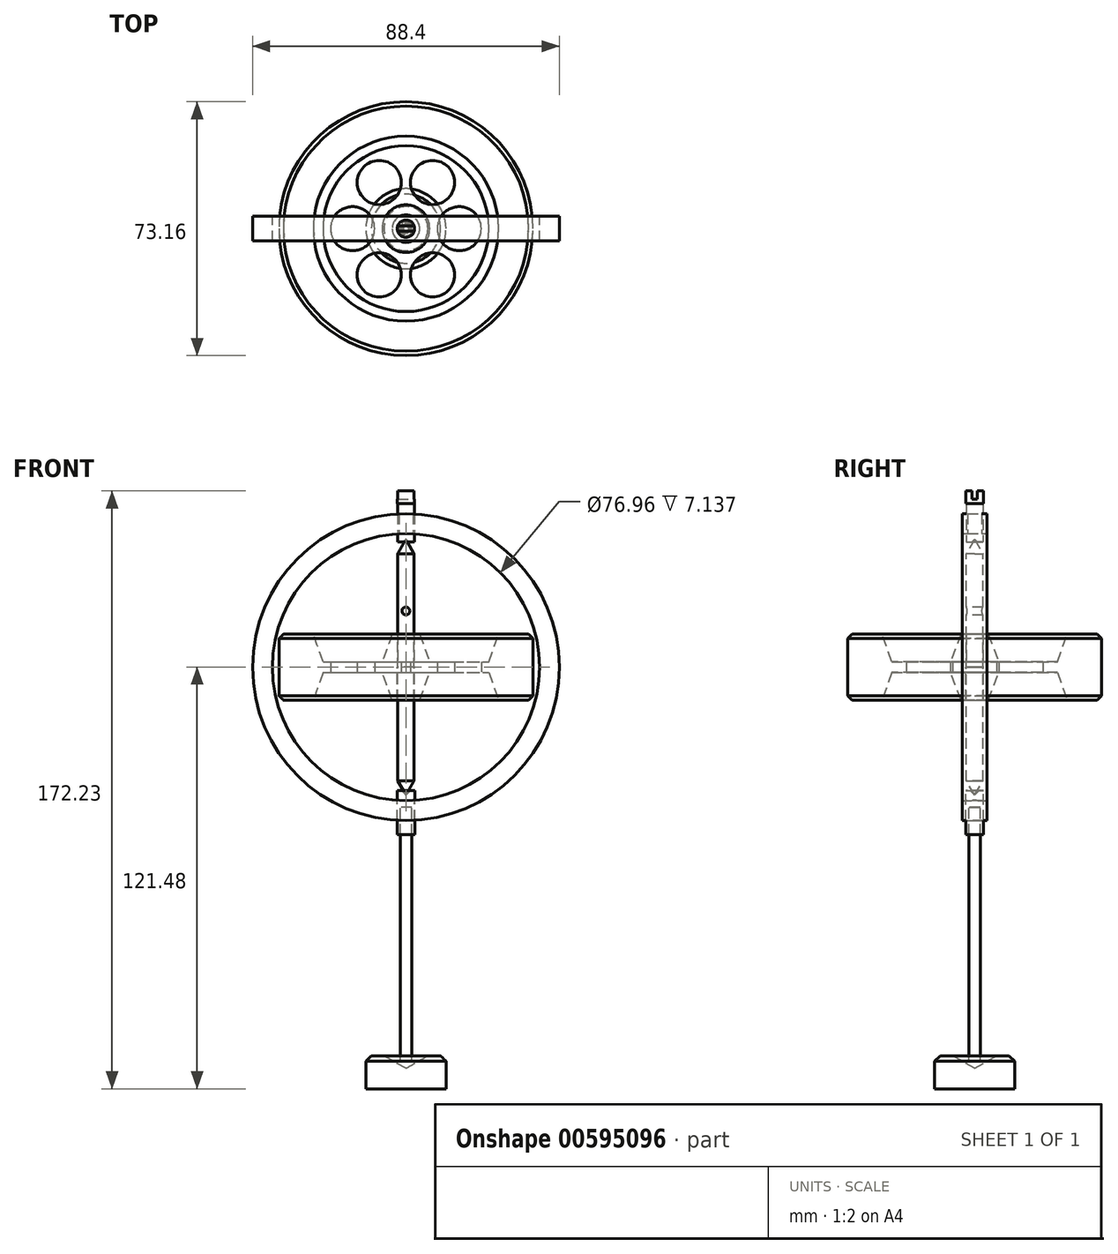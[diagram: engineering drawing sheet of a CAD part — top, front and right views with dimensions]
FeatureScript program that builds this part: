
annotation { "Feature Type Name" : "Feature", "Feature Type Description" : "" }
export const myFeature = defineFeature(function(context is Context, id is Id, definition is map)
    precondition{}
    {
        {
            var Q0;
            Q0=qCreatedBy(makeId("Front.planeOp"),FACE);
            var sketch = newSketch(context, id + "F0", { "sketchPlane" : qUnion([Q0])});
            skLineSegment(sketch, "E0.bottom", {"start": v(0, -9.52) * mm, "end": v(36.58, -9.52) * mm, "construction": true});
            skLineSegment(sketch, "E0.top", {"start": v(0, 9.52) * mm, "end": v(36.58, 9.52) * mm, "construction": true});
            skLineSegment(sketch, "E0.left", {"start": v(0, -9.52) * mm, "end": v(0, 9.52) * mm, "construction": true});
            skLineSegment(sketch, "E0.right", {"start": v(36.58, -9.52) * mm, "end": v(36.58, 9.52) * mm});
            skLineSegment(sketch, "E1", {"start": v(0, 0) * mm, "end": v(36.58, 0) * mm, "construction": true});
            skLineSegment(sketch, "E2", {"start": v(6.86, 1.57) * mm, "end": v(6.86, -1.57) * mm, "construction": true});
            skPoint(sketch, "E3", {"position": v(6.86, 0) * mm});
            skLineSegment(sketch, "E4", {"start": v(6.86, -1.57) * mm, "end": v(3.96, -9.53) * mm});
            skLineSegment(sketch, "E5.MirrorCS", {"start": v(6.86, 1.57) * mm, "end": v(3.96, 9.52) * mm});
            skLineSegment(sketch, "E6", {"start": v(2.39, 9.52) * mm, "end": v(2.39, -9.52) * mm});
            skLineSegment(sketch, "E7", {"start": v(6.86, 1.57) * mm, "end": v(23.88, 1.57) * mm});
            skLineSegment(sketch, "E8", {"start": v(2.39, 9.52) * mm, "end": v(3.96, 9.52) * mm});
            skLineSegment(sketch, "E9", {"start": v(2.39, -9.52) * mm, "end": v(3.96, -9.52) * mm});
            skLineSegment(sketch, "E10", {"start": v(26.67, -9.52) * mm, "end": v(36.58, -9.52) * mm});
            skLineSegment(sketch, "E11", {"start": v(26.67, 9.52) * mm, "end": v(36.58, 9.52) * mm});
            skLineSegment(sketch, "E12", {"start": v(23.88, -1.57) * mm, "end": v(26.67, -9.53) * mm});
            skLineSegment(sketch, "E13", {"start": v(6.86, -1.57) * mm, "end": v(23.88, -1.57) * mm});
            skLineSegment(sketch, "E14", {"start": v(26.67, 9.52) * mm, "end": v(23.88, 1.57) * mm});
            skSolve(sketch);
        }
        {
            var Q0;
            Q0=makeQuery(id+"F0.imprint","IMPRINT",FACE,{"disambiguationData":[TD([[makeQuery(id+"F0.imprint","IMPRINT",EDGE,{"derivedFrom":sQuery(id+"F0.wireOp",EDGE,"E0.right")}),1.0]])]});
            var Q1;
            Q1=sQuery(id+"F0.wireOp",EDGE,"E0.left");
            revolve(context, id + "F1", {"entities" : qUnion([Q0]), "axis" : qUnion([Q1]), "revolveType" : RevolveType.FULL});
        }
        {
            var Q0;
            Q0=qCreatedBy(makeId("Top.planeOp"),FACE);
            var sketch = newSketch(context, id + "F2", { "sketchPlane" : qUnion([Q0])});
            skPoint(sketch, "E15.0", {"position": v(36.58, 0) * mm});
            skCircle(sketch, "E16.cCircle", {"center": v(0, 0) * mm, "radius": 36.58 * mm, "construction": true});
            skPoint(sketch, "E17.0", {"position": v(23.88, 0) * mm});
            skPoint(sketch, "E18.0", {"position": v(6.86, 0) * mm});
            skCircle(sketch, "E19.cCircle", {"center": v(0, 0) * mm, "radius": 31.68 * mm, "construction": true});
            skLineSegment(sketch, "E19.0", {"start": v(36.58, 0) * mm, "end": v(18.29, -31.68) * mm, "construction": true});
            skLineSegment(sketch, "E19.1", {"start": v(18.29, -31.68) * mm, "end": v(-18.29, -31.68) * mm, "construction": true});
            skLineSegment(sketch, "E19.2", {"start": v(-18.29, -31.68) * mm, "end": v(-36.58, 0) * mm, "construction": true});
            skLineSegment(sketch, "E19.3", {"start": v(-36.58, 0) * mm, "end": v(-18.29, 31.68) * mm, "construction": true});
            skLineSegment(sketch, "E19.4", {"start": v(-18.29, 31.68) * mm, "end": v(18.29, 31.68) * mm, "construction": true});
            skLineSegment(sketch, "E19.5", {"start": v(18.29, 31.68) * mm, "end": v(36.58, 0) * mm, "construction": true});
            skPoint(sketch, "E19.0.midPoint", {"position": v(27.43, -15.84) * mm});
            skLineSegment(sketch, "E20", {"start": v(0, 0) * mm, "end": v(36.58, 0) * mm, "construction": true});
            skCircle(sketch, "E21", {"center": v(15.37, 0) * mm, "radius": 6.35 * mm});
            skLineSegment(sketch, "E22", {"start": v(6.86, 0) * mm, "end": v(23.88, 0) * mm, "construction": true});
            skCircle(sketch, "E23.1.0", {"center": v(7.68, 13.3) * mm, "radius": 6.35 * mm});
            skCircle(sketch, "E23.2.0", {"center": v(-7.68, 13.3) * mm, "radius": 6.35 * mm});
            skCircle(sketch, "E23.3.0", {"center": v(-15.37, 0) * mm, "radius": 6.35 * mm});
            skCircle(sketch, "E23.4.0", {"center": v(-7.68, -13.3) * mm, "radius": 6.35 * mm});
            skCircle(sketch, "E23.5.0", {"center": v(7.68, -13.3) * mm, "radius": 6.35 * mm});
            skSolve(sketch);
        }
        {
            var Q0;
            Q0 = qSketchRegion(id + "F2", true);
            extrude(context, id + "F3", {"entities" : qUnion([Q0]), "operationType" : NewBodyOperationType.REMOVE, "endBound" : BoundingType.THROUGH_ALL, "depth" : 25.4 * mm, "offsetDistance" : 25.4 * mm, "hasSecondDirection" : true, "secondDirectionBound" : SecondDirectionBoundingType.THROUGH_ALL, "secondDirectionOppositeDirection" : true, "secondDirectionDepth" : 25.4 * mm});
        }
        {
            var Q0;
            Q0=qCreatedBy(makeId("Front.planeOp"),FACE);
            var sketch = newSketch(context, id + "F4", { "sketchPlane" : qUnion([Q0])});
            skCircle(sketch, "E24", {"center": v(0, 0) * mm, "radius": 44.2 * mm});
            skCircle(sketch, "E25", {"center": v(0, 0) * mm, "radius": 38.48 * mm});
            skSolve(sketch);
        }
        {
            var Q0;
            Q0=makeQuery(id+"F4.imprint","IMPRINT",FACE,{"disambiguationData":[TD([[makeQuery(id+"F4.imprint","IMPRINT",EDGE,{"derivedFrom":sQuery(id+"F4.wireOp",EDGE,"E24")}),1.0]])]});
            extrude(context, id + "F5", {"entities" : qUnion([Q0]), "endBound" : BoundingType.SYMMETRIC, "depth" : 7.14 * mm, "offsetDistance" : 25.4 * mm});
        }
        {
            var Q0;
            Q0=qCreatedBy(makeId("Top.planeOp"),FACE);
            var sketch = newSketch(context, id + "F6", { "sketchPlane" : qUnion([Q0])});
            skCircle(sketch, "E26", {"center": v(0, 0) * mm, "radius": 2.5 * mm});
            skSolve(sketch);
        }
        {
            var Q0;
            Q0 = qSketchRegion(id + "F6", true);
            extrude(context, id + "F7", {"entities" : qUnion([Q0]), "operationType" : NewBodyOperationType.REMOVE, "endBound" : BoundingType.THROUGH_ALL, "oppositeDirection" : true, "depth" : 25.4 * mm, "offsetDistance" : 25.4 * mm});
        }
        {
            var Q0;
            Q0=qCreatedBy(makeId("Top.planeOp"),FACE);
            var sketch = newSketch(context, id + "F8", { "sketchPlane" : qUnion([Q0])});
            skCircle(sketch, "E27", {"center": v(0, 0) * mm, "radius": 2.02 * mm});
            skSolve(sketch);
        }
        {
            var Q0;
            Q0 = qSketchRegion(id + "F8", true);
            extrude(context, id + "F9", {"entities" : qUnion([Q0]), "operationType" : NewBodyOperationType.REMOVE, "endBound" : BoundingType.THROUGH_ALL, "depth" : 25.4 * mm, "offsetDistance" : 25.4 * mm});
        }
        {
            var Q0;
            Q0=makeQuery(id+"F1.opRevolve","SWEPT_EDGE",EDGE,{"disambiguationData":[OSD([sQuery(id+"F0.wireOp",EDGE,"E0.right"),sQuery(id+"F0.wireOp",EDGE,"E11")])]});
            var Q1;
            Q1=makeQuery(id+"F1.opRevolve","SWEPT_EDGE",EDGE,{"disambiguationData":[OSD([sQuery(id+"F0.wireOp",EDGE,"E0.right"),sQuery(id+"F0.wireOp",EDGE,"E10")])]});
            chamfer(context, id + "F10", {"entities" : qUnion([Q0, Q1]), "width" : 1.27 * mm, "tangentPropagation" : true});
        }
        {
            var Q0;
            Q0=qCreatedBy(makeId("Front.planeOp"),FACE);
            var sketch = newSketch(context, id + "F11", { "sketchPlane" : qUnion([Q0])});
            skLineSegment(sketch, "E28.0", {"start": v(2.39, 9.52) * mm, "end": v(-2.39, 9.52) * mm, "construction": true});
            skLineSegment(sketch, "E29.left", {"start": v(0, 36.83) * mm, "end": v(0, -36.83) * mm});
            skLineSegment(sketch, "E29.right", {"start": v(2.39, 32.7) * mm, "end": v(2.39, -32.7) * mm});
            skLineSegment(sketch, "E30", {"start": v(0, 36.83) * mm, "end": v(2.39, 32.7) * mm});
            skLineSegment(sketch, "E31", {"start": v(0, -36.83) * mm, "end": v(2.39, -32.7) * mm});
            skSolve(sketch);
        }
        {
            var Q0;
            Q0=makeQuery(id+"F11.imprint","IMPRINT",FACE,{"disambiguationData":[TD([[makeQuery(id+"F11.imprint","IMPRINT",EDGE,{"derivedFrom":sQuery(id+"F11.wireOp",EDGE,"E29.left")}),1.0]])]});
            var Q1;
            Q1=sQuery(id+"F11.wireOp",EDGE,"E29.left");
            revolve(context, id + "F12", {"entities" : qUnion([Q0]), "axis" : qUnion([Q1]), "revolveType" : RevolveType.FULL});
        }
        {
            var Q0;
            Q0=qCreatedBy(makeId("Front.planeOp"),FACE);
            var sketch = newSketch(context, id + "F13", { "sketchPlane" : qUnion([Q0])});
            skPoint(sketch, "E32.0", {"position": v(0, 36.83) * mm});
            skPoint(sketch, "E33.0", {"position": v(0, -36.83) * mm});
            skCircle(sketch, "E34", {"center": v(0, 16.18) * mm, "radius": 1.14 * mm});
            skSolve(sketch);
        }
        {
            var Q0;
            Q0 = qSketchRegion(id + "F13", true);
            extrude(context, id + "F14", {"entities" : qUnion([Q0]), "operationType" : NewBodyOperationType.REMOVE, "oppositeDirection" : true, "depth" : 25.4 * mm, "offsetDistance" : 25.4 * mm, "hasSecondDirection" : true, "secondDirectionOppositeDirection" : false, "secondDirectionDepth" : 25.4 * mm});
        }
        {
            var Q0;
            Q0=qCreatedBy(makeId("Front.planeOp"),FACE);
            var sketch = newSketch(context, id + "F15", { "sketchPlane" : qUnion([Q0])});
            skPoint(sketch, "E35.0", {"position": v(0, -36.83) * mm});
            skLineSegment(sketch, "E36.bottom", {"start": v(0, -35.56) * mm, "end": v(2.54, -35.56) * mm});
            skLineSegment(sketch, "E36.top", {"start": v(0, -48.26) * mm, "end": v(2.54, -48.26) * mm});
            skLineSegment(sketch, "E36.left", {"start": v(0, -35.56) * mm, "end": v(0, -48.26) * mm});
            skLineSegment(sketch, "E36.right", {"start": v(2.54, -35.56) * mm, "end": v(2.54, -48.26) * mm});
            skLineSegment(sketch, "E37", {"start": v(0, -40.39) * mm, "end": v(1.65, -40.39) * mm});
            skLineSegment(sketch, "E38", {"start": v(1.65, -40.39) * mm, "end": v(1.65, -48.26) * mm});
            skLineSegment(sketch, "E39", {"start": v(0, -36.83) * mm, "end": v(1.27, -35.56) * mm});
            skSolve(sketch);
        }
        {
            var Q0;
            {var subQ0=sQuery(id+"F15.wireOp",EDGE,"E36.right");Q0=makeQuery(id+"F15.imprint","IMPRINT",FACE,{"disambiguationData":[TD([[makeQuery(id+"F15.imprint","IMPRINT",EDGE,{"derivedFrom":subQ0}),-1.0]])]});}
            var Q1;
            Q1=sQuery(id+"F15.wireOp",EDGE,"E36.left");
            revolve(context, id + "F16", {"entities" : qUnion([Q0]), "axis" : qUnion([Q1]), "revolveType" : RevolveType.FULL});
        }
        {
            var Q0;
            Q0=qCreatedBy(makeId("Front.planeOp"),FACE);
            var sketch = newSketch(context, id + "F17", { "sketchPlane" : qUnion([Q0])});
            skPoint(sketch, "E40.0", {"position": v(0, 36.83) * mm});
            skLineSegment(sketch, "E41.bottom", {"start": v(0, 36.04) * mm, "end": v(2.5, 36.04) * mm});
            skLineSegment(sketch, "E41.top", {"start": v(0, 50.75) * mm, "end": v(2.5, 50.75) * mm});
            skLineSegment(sketch, "E41.left", {"start": v(0, 36.04) * mm, "end": v(0, 50.75) * mm});
            skLineSegment(sketch, "E41.right", {"start": v(2.5, 36.04) * mm, "end": v(2.5, 50.75) * mm});
            skLineSegment(sketch, "E42", {"start": v(2.5, 47.17) * mm, "end": v(2.41, 47.17) * mm});
            skLineSegment(sketch, "E43", {"start": v(2.41, 47.17) * mm, "end": v(2.41, 36.04) * mm});
            skLineSegment(sketch, "E44", {"start": v(0, 36.83) * mm, "end": v(0.79, 36.04) * mm});
            skSolve(sketch);
        }
        {
            var Q0;
            {var subQ1=sQuery(id+"F17.wireOp",EDGE,"E41.top");Q0=makeQuery(id+"F17.imprint","IMPRINT",FACE,{"disambiguationData":[TD([[makeQuery(id+"F17.imprint","IMPRINT",EDGE,{"derivedFrom":subQ1}),-1.0]])]});}
            var Q1;
            Q1=sQuery(id+"F17.wireOp",EDGE,"E41.left");
            revolve(context, id + "F18", {"entities" : qUnion([Q0]), "axis" : qUnion([Q1]), "revolveType" : RevolveType.FULL});
        }
        {
            var Q0;
            Q0=makeQuery(id+"F16.opRevolve","SWEPT_FACE",FACE,{"disambiguationData":[OSD([sQuery(id+"F15.wireOp",EDGE,"E37")])]});
            extrude(context, id + "F19", {"entities" : qUnion([Q0]), "depth" : 73.15 * mm, "offsetDistance" : 25.4 * mm});
        }
        {
            var Q0;
            Q0=qCreatedBy(makeId("Front.planeOp"),FACE);
            var sketch = newSketch(context, id + "F20", { "sketchPlane" : qUnion([Q0])});
            skLineSegment(sketch, "E45.0", {"start": v(-1.65, -113.54) * mm, "end": v(1.65, -113.54) * mm, "construction": true});
            skPoint(sketch, "E46", {"position": v(0, -113.54) * mm});
            skLineSegment(sketch, "E47.bottom", {"start": v(0, -111.95) * mm, "end": v(-11.55, -111.95) * mm});
            skLineSegment(sketch, "E47.top", {"start": v(0, -121.48) * mm, "end": v(-11.55, -121.48) * mm});
            skLineSegment(sketch, "E47.left", {"start": v(0, -111.95) * mm, "end": v(0, -121.48) * mm});
            skLineSegment(sketch, "E47.right", {"start": v(-11.55, -111.95) * mm, "end": v(-11.55, -121.48) * mm});
            skLineSegment(sketch, "E48", {"start": v(-9.96, -111.95) * mm, "end": v(-11.55, -113.54) * mm});
            skLineSegment(sketch, "E49", {"start": v(0, -115.62) * mm, "end": v(-6.35, -111.95) * mm});
            skSolve(sketch);
        }
        {
            var Q0;
            {var subQ1=sQuery(id+"F20.wireOp",EDGE,"E47.top");Q0=makeQuery(id+"F20.imprint","IMPRINT",FACE,{"disambiguationData":[TD([[makeQuery(id+"F20.imprint","IMPRINT",EDGE,{"derivedFrom":subQ1}),-1.0]])]});}
            var Q1;
            Q1=sQuery(id+"F20.wireOp",EDGE,"E47.left");
            revolve(context, id + "F21", {"entities" : qUnion([Q0]), "axis" : qUnion([Q1]), "revolveType" : RevolveType.FULL});
        }
        {
            var Q0;
            Q0=makeQuery(id+"F18.opRevolve","SWEPT_FACE",FACE,{"disambiguationData":[OSD([sQuery(id+"F17.wireOp",EDGE,"E41.top")])]});
            var sketch = newSketch(context, id + "F22", { "sketchPlane" : qUnion([Q0])});
            skLineSegment(sketch, "E50.bottom", {"start": v(-2.93, 0.76) * mm, "end": v(2.93, 0.76) * mm});
            skLineSegment(sketch, "E50.top", {"start": v(-2.93, -0.76) * mm, "end": v(2.93, -0.76) * mm});
            skLineSegment(sketch, "E50.left", {"start": v(-2.93, 0.76) * mm, "end": v(-2.93, -0.76) * mm});
            skLineSegment(sketch, "E50.right", {"start": v(2.93, 0.76) * mm, "end": v(2.93, -0.76) * mm});
            skPoint(sketch, "E50.middle", {"position": v(0, 0) * mm});
            skSolve(sketch);
        }
        {
            var Q0;
            Q0 = qSketchRegion(id + "F22", true);
            extrude(context, id + "F23", {"entities" : qUnion([Q0]), "operationType" : NewBodyOperationType.REMOVE, "oppositeDirection" : true, "depth" : 2.4 * mm, "offsetDistance" : 25.4 * mm});
        }
    });
